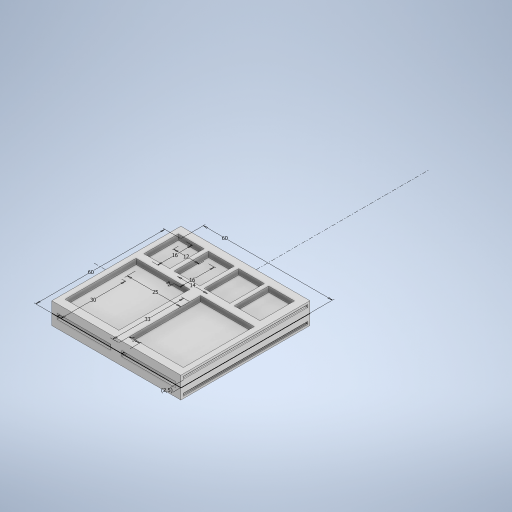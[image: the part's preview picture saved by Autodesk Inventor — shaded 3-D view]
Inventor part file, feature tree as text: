
AUTODESK INVENTOR PART (.ipt)
format: ipt  version: 2023 (Build 270158000, 158)  size: 461,824 bytes
history: native  units: mm
features: extrude x10, sketch x2
ambient origin geometry x8: Origin, YZ Plane, XZ Plane, XY Plane, X Axis, Y Axis, Z Axis, Center Point
bodies: Solido1 (feature_tree)
feature tree (12):
  sketch  "Schizzo1"
  extrude  "Estrusione1"  Depth=25.0mm
  extrude  "Estrusione2"  Depth=33.0mm
  extrude  "Estrusione10"  Depth=12.0mm
  extrude  "Estrusione11"  Depth=60.0mm
  extrude  "Estrusione12"  Depth=10.0mm TaperAngle=0.0deg
  extrude  "Estrusione13"  Depth=5.0mm TaperAngle=0.0deg
  sketch  "Schizzo5"
  extrude  "Estrusione14"  Depth=30.0mm
  extrude  "Estrusione15"  Depth=16.0mm
  extrude  "Estrusione18"  Depth=60.0mm
  extrude  "Estrusione19"  Depth=2.0mm
